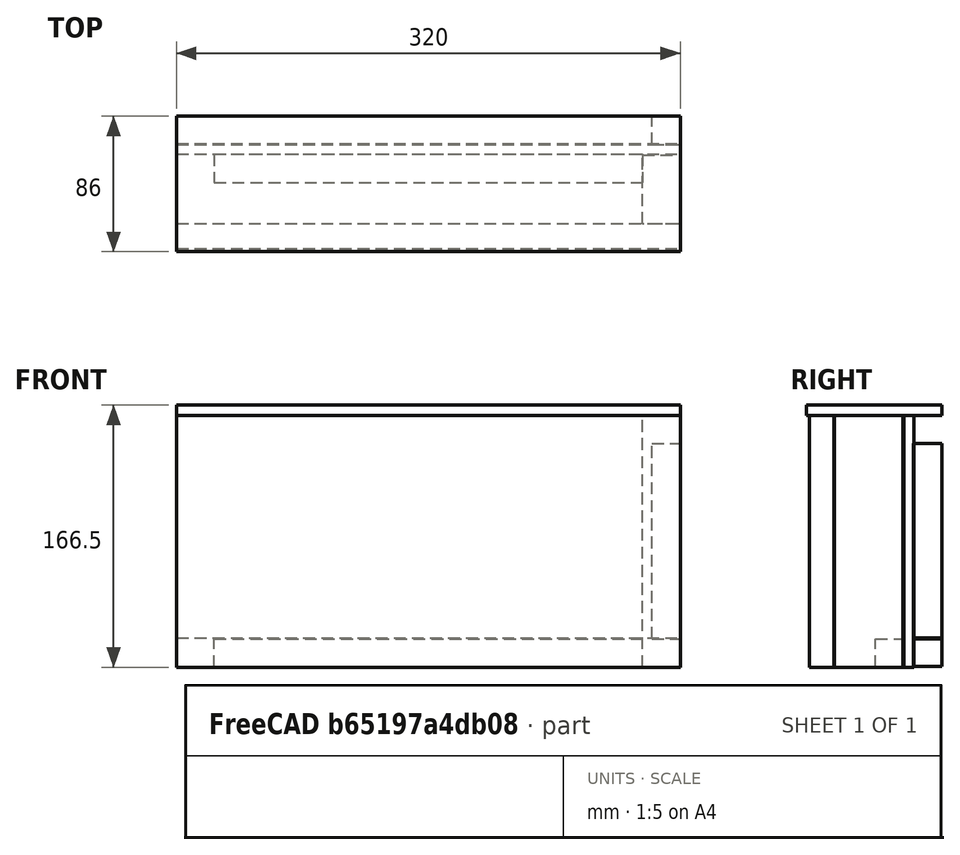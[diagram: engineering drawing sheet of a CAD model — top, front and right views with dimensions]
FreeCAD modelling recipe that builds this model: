
FCSTD DOCUMENT  (FreeCAD 0.21R33694 (Git))
Label: enclosure
License: All rights reserved
LicenseURL: http://en.wikipedia.org/wiki/All_rights_reserved
objects: TechDraw::DrawViewDimension×12, PartDesign::Body×11, Sketcher::SketchObject×7, PartDesign::Pad×7, TechDraw::DrawViewPart×7, PartDesign::FeatureBase×4, TechDraw::DrawSVGTemplate×1, TechDraw::DrawPage×1
note: 36 computed .brp shape members not serialized (recipe doc carries the construction recipe); baked Part::Feature solids carry a one-line shape summary decoded from their .brp

FEATURE [Sketcher::SketchObject] Sketch
  FullyConstrained = true
  MapMode = 5
  Placement = pos=(0,0,0) rot=(0.57735,0.57735,0.57735;2.0944rad)
  Support = -> [YZ_Plane]
  sketch-geometry (14):
    g0: LineSegment StartX=86 StartY=0 StartZ=0 EndX=86 EndY=6.5 EndZ=0
    g1: LineSegment StartX=0 StartY=6.5 StartZ=0 EndX=0 EndY=0 EndZ=0
    g2: LineSegment StartX=61.5 StartY=6.5 StartZ=0 EndX=43.5 EndY=6.5 EndZ=0
    g3: LineSegment StartX=86 StartY=6.5 StartZ=0 EndX=68 EndY=6.5 EndZ=0
    g4: LineSegment StartX=68 StartY=6.5 StartZ=0 EndX=61.5 EndY=6.5 EndZ=0
    g5: LineSegment StartX=43.5 StartY=0 StartZ=0 EndX=61.5 EndY=0 EndZ=0
    g6: LineSegment StartX=61.5 StartY=0 StartZ=0 EndX=68 EndY=0 EndZ=0
    g7: LineSegment StartX=68 StartY=0 StartZ=0 EndX=86 EndY=0 EndZ=0
    g8: LineSegment StartX=43.5 StartY=6.5 StartZ=0 EndX=17.5 EndY=6.5 EndZ=0
    g9: LineSegment StartX=17.5 StartY=6.5 StartZ=0 EndX=1.5 EndY=6.5 EndZ=0
    g10: LineSegment StartX=1.5 StartY=6.5 StartZ=0 EndX=0 EndY=6.5 EndZ=0
    g11: LineSegment StartX=17.5 StartY=0 StartZ=0 EndX=43.5 EndY=0 EndZ=0
    g12: LineSegment StartX=0 StartY=0 StartZ=0 EndX=1.5 EndY=0 EndZ=0
    g13: LineSegment StartX=1.5 StartY=0 StartZ=0 EndX=17.5 EndY=0 EndZ=0
  constraints (41):
    c: Coincident(g7,g0)
    c: Coincident(g0,g3)
    c: Coincident(g10,g1)
    c: Coincident(g1,g12)
    c: Vertical(g0)
    c: Vertical(g1)
    c: DistanceY(g0,g0) = 6.5
    c: DistanceX(g12,g7) = 86
    c: Coincident(g12,g-1)
    c: Coincident(g2,g8)
    c: Distance(g2,g0) = 42.5
    c: Coincident(g4,g2)
    c: Horizontal(g2)
    c: Coincident(g3,g4)
    c: Horizontal(g3)
    c: Horizontal(g4)
    c: Distance(g2,g0) = 24.5
    c: Distance(g3,g0) = 18
    c: Coincident(g11,g5)
    c: Coincident(g5,g6)
    c: Horizontal(g5)
    c: Coincident(g6,g7)
    c: Horizontal(g6)
    c: Horizontal(g7)
    c: Distance(g11,g0) = 42.5
    c: Distance(g5,g0) = 24.5
    c: Distance(g6,g0) = 18
    c: Coincident(g8,g9)
    c: Horizontal(g8)
    c: Coincident(g9,g10)
    c: Horizontal(g9)
    c: Horizontal(g10)
    c: Distance(g9,g1) = 1.5
    c: Distance(g1,g8) = 17.5
    c: Coincident(g13,g11)
    c: Horizontal(g11)
    c: Coincident(g12,g13)
    c: Horizontal(g12)
    c: Horizontal(g13)
    c: Distance(g1,g12) = 1.5
    c: Distance(g1,g11) = 17.5
FEATURE [PartDesign::Pad] Pad
  Direction = (1,-2e-16,3e-16)
  Length = 320
  Length2 = 10
  Placement = pos=(0,0,0) rot=(1,1,1;2.0944rad)
  Profile = -> Sketch
  ReferenceAxis = -> Sketch [N_Axis]
  Type = 0
FEATURE [PartDesign::Body] Body  label="Top"
  Group = -> [Sketch,Pad]
  Origin = -> Origin
  Placement = pos=(3.6e-15,7.1e-15,-0.5) rot=(0,0,1;0rad)
  Tip = -> Pad
FEATURE [PartDesign::FeatureBase] Clone
  BaseFeature = -> Body
FEATURE [PartDesign::Body] Body001  label="Bottom"
  Group = -> [Clone]
  Origin = -> Origin001
  Placement = pos=(0,0,166) rot=(0,0,1;0rad)
  Tip = -> Clone
FEATURE [Sketcher::SketchObject] Sketch001
  ExternalGeometry = -> [Pad]
  FullyConstrained = true
  MapMode = 5
  Support = -> [XY_Plane002]
  sketch-geometry (5):
    g0: LineSegment StartX=24 StartY=1.07e-14 StartZ=0 EndX=1.07e-14 EndY=1.07e-14 EndZ=0
    g1: LineSegment StartX=1.07e-14 StartY=1.07e-14 StartZ=0 EndX=1.07e-14 EndY=44 EndZ=0
    g2: LineSegment StartX=1.07e-14 StartY=44 StartZ=0 EndX=24 EndY=44 EndZ=0
    g3: LineSegment StartX=24 StartY=44 StartZ=0 EndX=24 EndY=26 EndZ=0
    g4: LineSegment StartX=24 StartY=26 StartZ=0 EndX=24 EndY=1.07e-14 EndZ=0
  constraints (15):
    c: Coincident(g0,g1)
    c: Coincident(g1,g2)
    c: Coincident(g2,g3)
    c: Coincident(g4,g0)
    c: Horizontal(g0)
    c: Horizontal(g2)
    c: Vertical(g1)
    c: DistanceX(g2,g2) = 24
    c: DistanceY(g1,g1) = 44
    c: Vertical(g1,g-3)
    c: Distance(g-3,g1) = 24
    c: Coincident(g3,g4)
    c: Vertical(g3)
    c: Vertical(g4)
    c: Distance(g2,g3) = 18
FEATURE [PartDesign::Pad] Pad001
  Direction = (0,0,1)
  Length = 160
  Length2 = 10
  Profile = -> Sketch001
  ReferenceAxis = -> Sketch001 [N_Axis]
  Type = 0
FEATURE [PartDesign::Body] Body002  label="RightPillar"
  Group = -> [Sketch001,Pad001]
  Origin = -> Origin002
  Placement = pos=(3e-15,17.5,6) rot=(0,0,1;0rad)
  Tip = -> Pad001
FEATURE [PartDesign::FeatureBase] Clone001
  BaseFeature = -> Body002
  Placement = pos=(296,17.5,6) rot=(0,0,1;0rad)
FEATURE [PartDesign::Body] Body003  label="LeftPillar"
  Group = -> [Clone001]
  Origin = -> Origin003
  Tip = -> Clone001
FEATURE [Sketcher::SketchObject] Sketch002
  ExternalGeometry = -> [Pad001]
  FullyConstrained = true
  MapMode = 5
  Placement = pos=(0,0,0) rot=(0.57735,0.57735,0.57735;2.0944rad)
  Support = -> [YZ_Plane004]
  sketch-geometry (4):
    g0: LineSegment StartX=50 StartY=142 StartZ=0 EndX=68 EndY=142 EndZ=0
    g1: LineSegment StartX=68 StartY=142 StartZ=0 EndX=68 EndY=160 EndZ=0
    g2: LineSegment StartX=68 StartY=160 StartZ=0 EndX=50 EndY=160 EndZ=0
    g3: LineSegment StartX=50 StartY=160 StartZ=0 EndX=50 EndY=142 EndZ=0
  constraints (12):
    c: Coincident(g0,g1)
    c: Coincident(g1,g2)
    c: Coincident(g2,g3)
    c: Coincident(g3,g0)
    c: Horizontal(g0)
    c: Horizontal(g2)
    c: Vertical(g1)
    c: Vertical(g3)
    c: DistanceY(g1,g1) = 18
    c: DistanceX(g0,g0) = 18
    c: Horizontal(g2,g-3)
    c: Distance(g2,g-3) = 6
FEATURE [PartDesign::Pad] Pad002
  Direction = (1,-2e-16,3e-16)
  Length = 320
  Length2 = 10
  Placement = pos=(0,0,0) rot=(1,1,1;2.0944rad)
  Profile = -> Sketch002
  ReferenceAxis = -> Sketch002 [N_Axis]
  Type = 0
FEATURE [PartDesign::Body] Body004  label="BottomEdge"
  Group = -> [Sketch002,Pad002]
  Origin = -> Origin004
  Placement = pos=(5.68e-14,18,6) rot=(0,0,1;0rad)
  Tip = -> Pad002
FEATURE [PartDesign::FeatureBase] Clone002
  BaseFeature = -> Body004
  Placement = pos=(7.92e-14,18,-135.5) rot=(0,0,1;0rad)
FEATURE [PartDesign::Body] Body005  label="TopEdge"
  Group = -> [Clone002]
  Origin = -> Origin005
  Tip = -> Clone002
FEATURE [Sketcher::SketchObject] Sketch003
  FullyConstrained = true
  MapMode = 5
  Placement = pos=(0,0,0) rot=(0.57735,0.57735,0.57735;2.0944rad)
  Support = -> [YZ_Plane006]
  sketch-geometry (4):
    g0: LineSegment StartX=62 StartY=0 StartZ=0 EndX=44 EndY=0 EndZ=0
    g1: LineSegment StartX=44 StartY=0 StartZ=0 EndX=44 EndY=18 EndZ=0
    g2: LineSegment StartX=44 StartY=18 StartZ=0 EndX=62 EndY=18 EndZ=0
    g3: LineSegment StartX=62 StartY=18 StartZ=0 EndX=62 EndY=0 EndZ=0
  constraints (12):
    c: Coincident(g0,g1)
    c: Coincident(g1,g2)
    c: Coincident(g2,g3)
    c: Coincident(g3,g0)
    c: Horizontal(g0)
    c: Horizontal(g2)
    c: Vertical(g1)
    c: Vertical(g3)
    c: DistanceX(g2,g2) = 18
    c: DistanceY(g3,g3) = 18
    c: Horizontal(g0,g-1)
    c: Distance(g-1,g0) = 44
FEATURE [PartDesign::Pad] Pad003
  Direction = (1,-2e-16,3e-16)
  Length = 272
  Length2 = 10
  Placement = pos=(0,0,0) rot=(0.57735,0.57735,0.57735;2.0944rad)
  Profile = -> Sketch003
  ReferenceAxis = -> Sketch003 [N_Axis]
  Type = 0
FEATURE [PartDesign::Body] Body006  label="TopInternalEdge"
  Group = -> [Sketch003,Pad003]
  Origin = -> Origin006
  Placement = pos=(24,-1.42e-14,6) rot=(0,0,1;0rad)
  Tip = -> Pad003
FEATURE [Sketcher::SketchObject] Sketch004
  FullyConstrained = true
  MapMode = 5
  Placement = pos=(0,0,0) rot=(0.57735,0.57735,0.57735;2.0944rad)
  Support = -> [YZ_Plane007]
  sketch-geometry (4):
    g0: LineSegment StartX=62 StartY=0 StartZ=0 EndX=68.5 EndY=0 EndZ=0
    g1: LineSegment StartX=68.5 StartY=0 StartZ=0 EndX=68.5 EndY=160 EndZ=0
    g2: LineSegment StartX=68.5 StartY=160 StartZ=0 EndX=62 EndY=160 EndZ=0
    g3: LineSegment StartX=62 StartY=160 StartZ=0 EndX=62 EndY=0 EndZ=0
  constraints (12):
    c: Coincident(g0,g1)
    c: Coincident(g1,g2)
    c: Coincident(g2,g3)
    c: Coincident(g3,g0)
    c: Horizontal(g0)
    c: Horizontal(g2)
    c: Vertical(g1)
    c: Vertical(g3)
    c: DistanceY(g1,g1) = 160
    c: DistanceX(g2,g2) = 6.5
    c: DistanceX(g0) = 62
    c: DistanceY(g0) = 0
FEATURE [PartDesign::Pad] Pad004
  Direction = (1,-2e-16,3e-16)
  Length = 320
  Length2 = 10
  Placement = pos=(0,0,0) rot=(1,1,1;2.0944rad)
  Profile = -> Sketch004
  ReferenceAxis = -> Sketch004 [N_Axis]
  Type = 0
FEATURE [PartDesign::Body] Body007  label="Back"
  Group = -> [Sketch004,Pad004]
  Origin = -> Origin007
  Placement = pos=(0,0,6) rot=(0,0,1;0rad)
  Tip = -> Pad004
FEATURE [Sketcher::SketchObject] Sketch005
  FullyConstrained = true
  MapMode = 5
  Placement = pos=(0,0,0) rot=(0.57735,0.57735,0.57735;2.0944rad)
  Support = -> [YZ_Plane008]
  sketch-geometry (4):
    g0: LineSegment StartX=68 StartY=18 StartZ=0 EndX=86 EndY=18 EndZ=0
    g1: LineSegment StartX=86 StartY=18 StartZ=0 EndX=86 EndY=142 EndZ=0
    g2: LineSegment StartX=86 StartY=142 StartZ=0 EndX=68 EndY=142 EndZ=0
    g3: LineSegment StartX=68 StartY=142 StartZ=0 EndX=68 EndY=18 EndZ=0
  constraints (12):
    c: Coincident(g0,g1)
    c: Coincident(g1,g2)
    c: Coincident(g2,g3)
    c: Coincident(g3,g0)
    c: Horizontal(g0)
    c: Horizontal(g2)
    c: Vertical(g1)
    c: Vertical(g3)
    c: DistanceY(g3,g3) = 124
    c: DistanceX(g0,g0) = 18
    c: DistanceX(g0) = 68
    c: DistanceY(g0) = 18
FEATURE [PartDesign::Pad] Pad005
  Direction = (1,-2e-16,3e-16)
  Length = 18
  Length2 = 10
  Placement = pos=(0,0,0) rot=(0.57735,0.57735,0.57735;2.0944rad)
  Profile = -> Sketch005
  ReferenceAxis = -> Sketch005 [N_Axis]
  Type = 0
FEATURE [PartDesign::Body] Body008  label="HandleRight"
  Group = -> [Sketch005,Pad005]
  Origin = -> Origin008
  Placement = pos=(-2.6e-14,-1.42e-14,6) rot=(0,0,1;0rad)
  Tip = -> Pad005
FEATURE [PartDesign::FeatureBase] Clone003
  BaseFeature = -> Body008
  Placement = pos=(0,-1.14e-13,0) rot=(0,0,1;0rad)
FEATURE [PartDesign::Body] Body009  label="HandleLeft"
  Group = -> [Clone003]
  Origin = -> Origin009
  Placement = pos=(302,-1.42e-14,6) rot=(0,0,1;0rad)
  Tip = -> Clone003
FEATURE [Sketcher::SketchObject] Sketch006
  FullyConstrained = true
  MapMode = 5
  Placement = pos=(0,0,0) rot=(0.57735,0.57735,0.57735;2.0944rad)
  Support = -> [YZ_Plane010]
  sketch-geometry (4):
    g0: LineSegment StartX=2 StartY=0 StartZ=0 EndX=18 EndY=0 EndZ=0
    g1: LineSegment StartX=18 StartY=0 StartZ=0 EndX=18 EndY=160 EndZ=0
    g2: LineSegment StartX=18 StartY=160 StartZ=0 EndX=2 EndY=160 EndZ=0
    g3: LineSegment StartX=2 StartY=160 StartZ=0 EndX=2 EndY=0 EndZ=0
  constraints (12):
    c: Coincident(g0,g1)
    c: Coincident(g1,g2)
    c: Coincident(g2,g3)
    c: Coincident(g3,g0)
    c: Horizontal(g0)
    c: Horizontal(g2)
    c: Vertical(g1)
    c: Vertical(g3)
    c: DistanceY(g1,g1) = 160
    c: DistanceX(g2,g2) = 16
    c: DistanceX(g0) = 2
    c: DistanceY(g0) = 0
FEATURE [PartDesign::Pad] Pad006
  Direction = (1,-2e-16,3e-16)
  Length = 320
  Length2 = 10
  Placement = pos=(0,0,0) rot=(0.57735,0.57735,0.57735;2.0944rad)
  Profile = -> Sketch006
  ReferenceAxis = -> Sketch006 [N_Axis]
  Type = 0
FEATURE [PartDesign::Body] Body010  label="P5Panel"
  Group = -> [Sketch006,Pad006]
  Origin = -> Origin010
  Placement = pos=(0,4e-15,6) rot=(0,0,1;0rad)
  Tip = -> Pad006
FEATURE [TechDraw::DrawSVGTemplate] Template
  Height = 297
  Orientation = 0
  Template = <path>
  Width = 210
FEATURE [TechDraw::DrawViewPart] View  label="Front"
  CoarseView = false
  Direction = (0.57735,-0.57735,-0.57735)
  Focus = 100
  HardHidden = false
  IsoCount = 0
  IsoHidden = false
  IsoVisible = false
  LockPosition = false
  Perspective = false
  Rotation = 0
  Scale = 0.25
  ScaleType = 2
  ScrubCount = 0
  SeamHidden = false
  SeamVisible = false
  SmoothHidden = false
  SmoothVisible = true
  Source = -> [Body010,Body,Body001,Body002,Body003,Body004,Body005,Body006,Body007,Body008,Body009]
  X = 46.3106
  XDirection = (-0.707107,-0.707107,0)
  Y = 252.421
FEATURE [TechDraw::DrawViewPart] View001  label="2x bottom/top panel"
  CoarseView = false
  Direction = (0,0,-1)
  Focus = 100
  HardHidden = false
  IsoCount = 0
  IsoHidden = false
  IsoVisible = false
  LockPosition = false
  Perspective = false
  Rotation = 0
  Scale = 0.25
  ScaleType = 2
  ScrubCount = 0
  SeamHidden = false
  SeamVisible = false
  SmoothHidden = false
  SmoothVisible = true
  Source = -> [Body]
  X = 106.39
  XDirection = (0,-1,0)
  Y = 152
FEATURE [TechDraw::DrawViewPart] View003  label="2x bottom/top edge"
  CoarseView = false
  Direction = (0,0,1)
  Focus = 100
  HardHidden = false
  IsoCount = 0
  IsoHidden = false
  IsoVisible = false
  LockPosition = false
  Perspective = false
  Rotation = 0
  Scale = 0.25
  ScaleType = 2
  ScrubCount = 0
  SeamHidden = false
  SeamVisible = false
  SmoothHidden = false
  SmoothVisible = true
  Source = -> [Body004]
  X = 65.9096
  XDirection = (0,-1,0)
  Y = 152
FEATURE [TechDraw::DrawViewPart] View004  label="1x top internal edge"
  CoarseView = false
  Direction = (0,0,1)
  Focus = 100
  HardHidden = false
  IsoCount = 0
  IsoHidden = false
  IsoVisible = false
  LockPosition = false
  Perspective = false
  Rotation = 0
  Scale = 0.25
  ScaleType = 2
  ScrubCount = 0
  SeamHidden = false
  SeamVisible = false
  SmoothHidden = false
  SmoothVisible = true
  Source = -> [Body006]
  X = 26.0776
  XDirection = (0,-1,0)
  Y = 152
FEATURE [TechDraw::DrawViewPart] View005  label="1x back panel"
  CoarseView = false
  Direction = (0,1,0)
  Focus = 100
  HardHidden = false
  IsoCount = 0
  IsoHidden = false
  IsoVisible = false
  LockPosition = false
  Perspective = false
  Rotation = 0
  Scale = 0.25
  ScaleType = 2
  ScrubCount = 0
  SeamHidden = false
  SeamVisible = false
  SmoothHidden = false
  SmoothVisible = true
  Source = -> [Body007]
  X = 158
  XDirection = (0,0,1)
  Y = 152
FEATURE [TechDraw::DrawViewPart] View006  label="2x left/right handle"
  CoarseView = false
  Direction = (0,1,0)
  Focus = 100
  HardHidden = false
  IsoCount = 0
  IsoHidden = false
  IsoVisible = false
  LockPosition = false
  Perspective = false
  Rotation = 0
  Scale = 0.25
  ScaleType = 2
  ScrubCount = 0
  SeamHidden = false
  SeamVisible = false
  SmoothHidden = false
  SmoothVisible = true
  Source = -> [Body008]
  X = 158
  XDirection = (0,0,1)
  Y = 219.377
FEATURE [TechDraw::DrawViewPart] View008  label="2x left/right edge"
  CoarseView = false
  Direction = (-1,0,0)
  Focus = 100
  HardHidden = false
  IsoCount = 0
  IsoHidden = false
  IsoVisible = false
  LockPosition = false
  Perspective = false
  Rotation = 0
  Scale = 0.25
  ScaleType = 2
  ScrubCount = 0
  SeamHidden = false
  SeamVisible = false
  SmoothHidden = false
  SmoothVisible = true
  Source = -> [Body002]
  X = 158
  XDirection = (0,0,1)
  Y = 249.748
FEATURE [TechDraw::DrawViewDimension] Dimension
  AngleOverride = false
  Arbitrary = false
  ArbitraryTolerances = false
  EqualTolerance = true
  ExtensionAngle = 0
  FormatSpec = %.2w
  FormatSpecOverTolerance = %+.2w
  FormatSpecUnderTolerance = %+.2w
  Inverted = false
  LineAngle = 0
  LockPosition = false
  MeasureType = 1
  OverTolerance = 0
  References2D = -> [View004]
  Rotation = 0
  ScaleType = 1
  TheoreticalExact = false
  Type = 2
  UnderTolerance = 0
  X = -9.49024
  Y = 1.45207
FEATURE [TechDraw::DrawViewDimension] Dimension001
  AngleOverride = false
  Arbitrary = false
  ArbitraryTolerances = false
  EqualTolerance = true
  ExtensionAngle = 0
  FormatSpec = %.2w
  FormatSpecOverTolerance = %+.2w
  FormatSpecUnderTolerance = %+.2w
  Inverted = false
  LineAngle = 0
  LockPosition = false
  MeasureType = 1
  OverTolerance = 0
  References2D = -> [View004]
  Rotation = 0
  ScaleType = 1
  TheoreticalExact = false
  Type = 1
  UnderTolerance = 0
  X = -0.190533
  Y = 45.7408
FEATURE [TechDraw::DrawViewDimension] Dimension002
  AngleOverride = false
  Arbitrary = false
  ArbitraryTolerances = false
  EqualTolerance = true
  ExtensionAngle = 0
  FormatSpec = %.2w
  FormatSpecOverTolerance = %+.2w
  FormatSpecUnderTolerance = %+.2w
  Inverted = false
  LineAngle = 0
  LockPosition = false
  MeasureType = 1
  OverTolerance = 0
  References2D = -> [View003]
  Rotation = 0
  ScaleType = 1
  TheoreticalExact = false
  Type = 1
  UnderTolerance = 0
  X = -0.190533
  Y = 51.5503
FEATURE [TechDraw::DrawViewDimension] Dimension003
  AngleOverride = false
  Arbitrary = false
  ArbitraryTolerances = false
  EqualTolerance = true
  ExtensionAngle = 0
  FormatSpec = %.2w
  FormatSpecOverTolerance = %+.2w
  FormatSpecUnderTolerance = %+.2w
  Inverted = false
  LineAngle = 0
  LockPosition = false
  MeasureType = 1
  OverTolerance = 0
  References2D = -> [View003]
  Rotation = 0
  ScaleType = 1
  TheoreticalExact = false
  Type = 2
  UnderTolerance = 0
  X = -9.39497
  Y = 3.0716
FEATURE [TechDraw::DrawViewDimension] Dimension004
  AngleOverride = false
  Arbitrary = false
  ArbitraryTolerances = false
  EqualTolerance = true
  ExtensionAngle = 0
  FormatSpec = %.2w
  FormatSpecOverTolerance = %+.2w
  FormatSpecUnderTolerance = %+.2w
  Inverted = false
  LineAngle = 0
  LockPosition = false
  MeasureType = 1
  OverTolerance = 0
  References2D = -> [View001]
  Rotation = 0
  ScaleType = 1
  TheoreticalExact = false
  Type = 2
  UnderTolerance = 0
  X = -17.895
  Y = 2.35115
FEATURE [TechDraw::DrawViewDimension] Dimension005
  AngleOverride = false
  Arbitrary = false
  ArbitraryTolerances = false
  EqualTolerance = true
  ExtensionAngle = 0
  FormatSpec = %.2w
  FormatSpecOverTolerance = %+.2w
  FormatSpecUnderTolerance = %+.2w
  Inverted = false
  LineAngle = 0
  LockPosition = false
  MeasureType = 1
  OverTolerance = 0
  References2D = -> [View001]
  Rotation = 0
  ScaleType = 1
  TheoreticalExact = false
  Type = 1
  UnderTolerance = 0
  X = 0.056187
  Y = 51.386
FEATURE [TechDraw::DrawViewDimension] Dimension006
  AngleOverride = false
  Arbitrary = false
  ArbitraryTolerances = false
  EqualTolerance = true
  ExtensionAngle = 0
  FormatSpec = %.2w
  FormatSpecOverTolerance = %+.2w
  FormatSpecUnderTolerance = %+.2w
  Inverted = false
  LineAngle = 0
  LockPosition = false
  MeasureType = 1
  OverTolerance = 0
  References2D = -> [View005]
  Rotation = 0
  ScaleType = 1
  TheoreticalExact = false
  Type = 2
  UnderTolerance = 0
  X = -28.4707
  Y = 2.64605
FEATURE [TechDraw::DrawViewDimension] Dimension007
  AngleOverride = false
  Arbitrary = false
  ArbitraryTolerances = false
  EqualTolerance = true
  ExtensionAngle = 0
  FormatSpec = %.2w
  FormatSpecOverTolerance = %+.2w
  FormatSpecUnderTolerance = %+.2w
  Inverted = false
  LineAngle = 0
  LockPosition = false
  MeasureType = 1
  OverTolerance = 0
  References2D = -> [View005]
  Rotation = 0
  ScaleType = 1
  TheoreticalExact = false
  Type = 1
  UnderTolerance = 0
  X = 0.360682
  Y = 51.1168
FEATURE [TechDraw::DrawViewDimension] Dimension008
  AngleOverride = false
  Arbitrary = false
  ArbitraryTolerances = false
  EqualTolerance = true
  ExtensionAngle = 0
  FormatSpec = %.2w
  FormatSpecOverTolerance = %+.2w
  FormatSpecUnderTolerance = %+.2w
  Inverted = false
  LineAngle = 0
  LockPosition = false
  MeasureType = 1
  OverTolerance = 0
  References2D = -> [View008]
  Rotation = 0
  ScaleType = 1
  TheoreticalExact = false
  Type = 1
  UnderTolerance = 0
  X = -1.44364
  Y = 17.1129
FEATURE [TechDraw::DrawViewDimension] Dimension009
  AngleOverride = false
  Arbitrary = false
  ArbitraryTolerances = false
  EqualTolerance = true
  ExtensionAngle = 0
  FormatSpec = %.2w
  FormatSpecOverTolerance = %+.2w
  FormatSpecUnderTolerance = %+.2w
  Inverted = false
  LineAngle = 0
  LockPosition = false
  MeasureType = 1
  OverTolerance = 0
  References2D = -> [View008]
  Rotation = 0
  ScaleType = 1
  TheoreticalExact = false
  Type = 2
  UnderTolerance = 0
  X = -29.7445
  Y = 3.22182
FEATURE [TechDraw::DrawViewDimension] Dimension010
  AngleOverride = false
  Arbitrary = false
  ArbitraryTolerances = false
  EqualTolerance = true
  ExtensionAngle = 0
  FormatSpec = %.2w
  FormatSpecOverTolerance = %+.2w
  FormatSpecUnderTolerance = %+.2w
  Inverted = false
  LineAngle = 0
  LockPosition = false
  MeasureType = 1
  OverTolerance = 0
  References2D = -> [View006]
  Rotation = 0
  ScaleType = 1
  TheoreticalExact = false
  Type = 1
  UnderTolerance = 0
  X = 0.360909
  Y = 13.5923
FEATURE [TechDraw::DrawViewDimension] Dimension011
  AngleOverride = false
  Arbitrary = false
  ArbitraryTolerances = false
  EqualTolerance = true
  ExtensionAngle = 0
  FormatSpec = %.2w
  FormatSpecOverTolerance = %+.2w
  FormatSpecUnderTolerance = %+.2w
  Inverted = false
  LineAngle = 0
  LockPosition = false
  MeasureType = 1
  OverTolerance = 0
  References2D = -> [View006]
  Rotation = 0
  ScaleType = 1
  TheoreticalExact = false
  Type = 2
  UnderTolerance = 0
  X = -24.6893
  Y = 2.86091
FEATURE [TechDraw::DrawPage] Page  label="components"
  KeepUpdated = true
  NextBalloonIndex = 1
  ProjectionType = 0
  Scale = 0.2
  Template = -> Template
  Views = -> [View,View001,View003,View004,View005,View006,View008,Dimension,Dimension001,Dimension002,Dimension003,Dimension004,Dimension005,Dimension006,Dimension007,Dimension008,Dimension009,Dimension010,Dimension011]
note: 1 file-system path scrubbed to <path> (originals preserved in the JSON sidecar)
